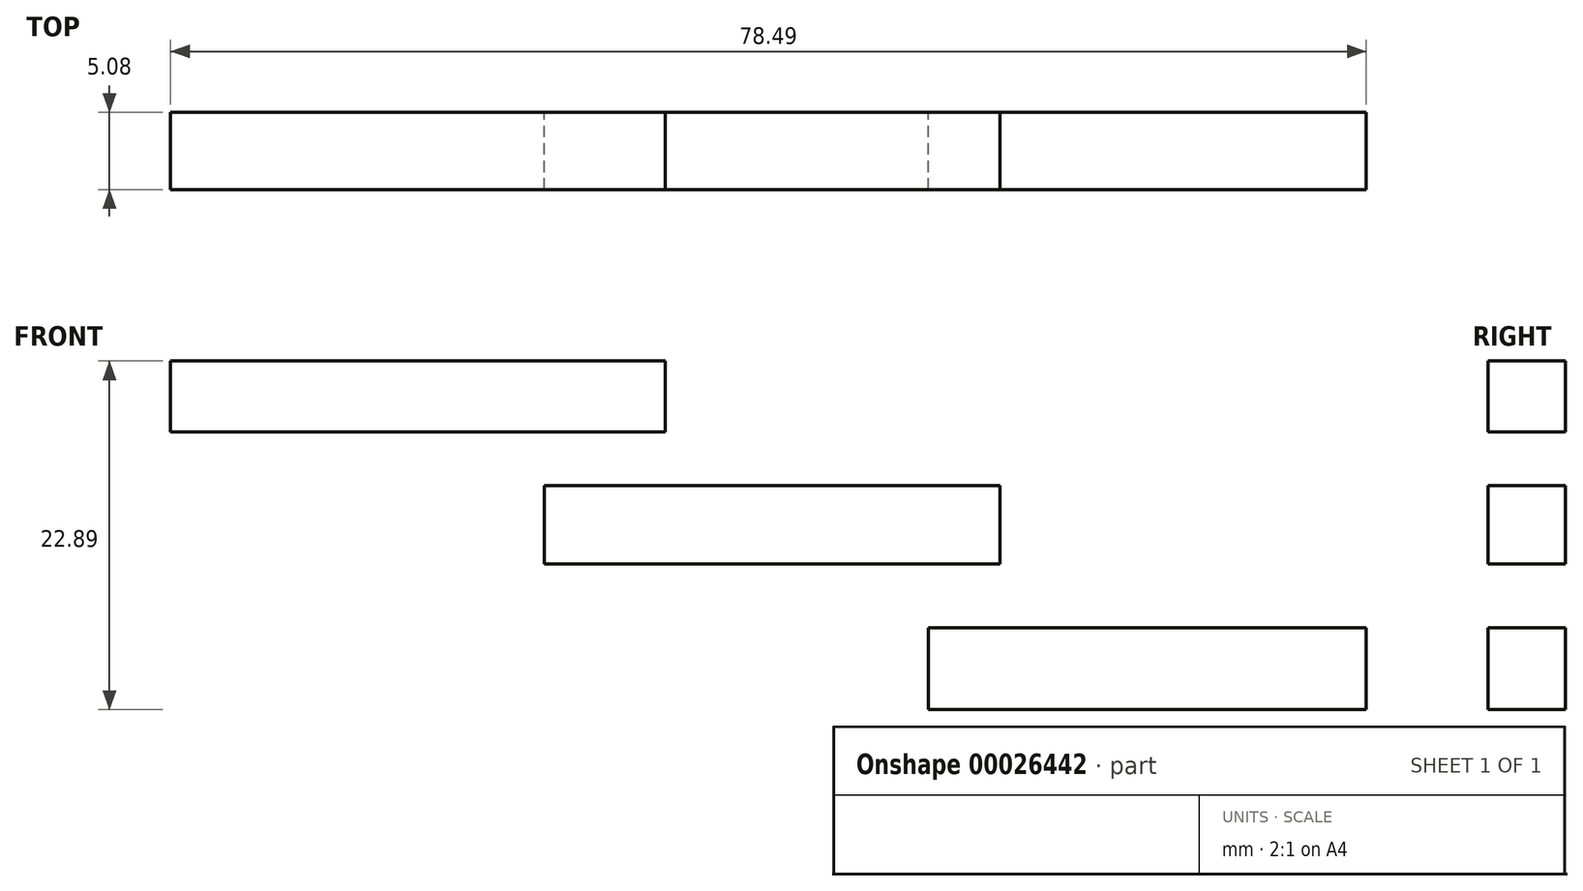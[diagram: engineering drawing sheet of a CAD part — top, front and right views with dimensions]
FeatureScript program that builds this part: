
annotation { "Feature Type Name" : "Feature", "Feature Type Description" : "" }
export const myFeature = defineFeature(function(context is Context, id is Id, definition is map)
    precondition{}
    {
        {
            var Q0;
            Q0=qCreatedBy(makeId("Front.planeOp"),FACE);
            var sketch = newSketch(context, id + "F0", { "sketchPlane" : qUnion([Q0])});
            skLineSegment(sketch, "E0.bottom", {"start": v(-49.76, 36.56) * mm, "end": v(-17.29, 36.56) * mm});
            skLineSegment(sketch, "E0.top", {"start": v(-49.76, 31.89) * mm, "end": v(-17.29, 31.89) * mm});
            skLineSegment(sketch, "E0.left", {"start": v(-49.76, 36.56) * mm, "end": v(-49.76, 31.89) * mm});
            skLineSegment(sketch, "E0.right", {"start": v(-17.29, 36.56) * mm, "end": v(-17.29, 31.89) * mm});
            skLineSegment(sketch, "E1.bottom", {"start": v(-25.23, 28.38) * mm, "end": v(4.67, 28.38) * mm});
            skLineSegment(sketch, "E1.top", {"start": v(-25.23, 23.24) * mm, "end": v(4.67, 23.24) * mm});
            skLineSegment(sketch, "E1.left", {"start": v(-25.23, 28.38) * mm, "end": v(-25.23, 23.24) * mm});
            skLineSegment(sketch, "E1.right", {"start": v(4.67, 28.38) * mm, "end": v(4.67, 23.24) * mm});
            skLineSegment(sketch, "E2.bottom", {"start": v(0, 19.04) * mm, "end": v(28.73, 19.04) * mm});
            skLineSegment(sketch, "E2.top", {"start": v(0, 13.67) * mm, "end": v(28.73, 13.67) * mm});
            skLineSegment(sketch, "E2.left", {"start": v(0, 19.04) * mm, "end": v(0, 13.67) * mm});
            skLineSegment(sketch, "E2.right", {"start": v(28.73, 19.04) * mm, "end": v(28.73, 13.67) * mm});
            skSolve(sketch);
        }
        {
            var Q0;
            Q0=makeQuery(id+"F0.imprint","IMPRINT",FACE,{"disambiguationData":[TD([[makeQuery(id+"F0.imprint","IMPRINT",EDGE,{"derivedFrom":sQuery(id+"F0.wireOp",EDGE,"E0.bottom")}),-1.0]])]});
            var Q1;
            Q1=makeQuery(id+"F0.imprint","IMPRINT",FACE,{"disambiguationData":[TD([[makeQuery(id+"F0.imprint","IMPRINT",EDGE,{"derivedFrom":sQuery(id+"F0.wireOp",EDGE,"E1.bottom")}),-1.0]])]});
            var Q2;
            Q2=makeQuery(id+"F0.imprint","IMPRINT",FACE,{"disambiguationData":[TD([[makeQuery(id+"F0.imprint","IMPRINT",EDGE,{"derivedFrom":sQuery(id+"F0.wireOp",EDGE,"E2.bottom")}),-1.0]])]});
            extrude(context, id + "F1", {"entities" : qUnion([Q0, Q1, Q2]), "depth" : 5.08 * mm});
        }
    });
